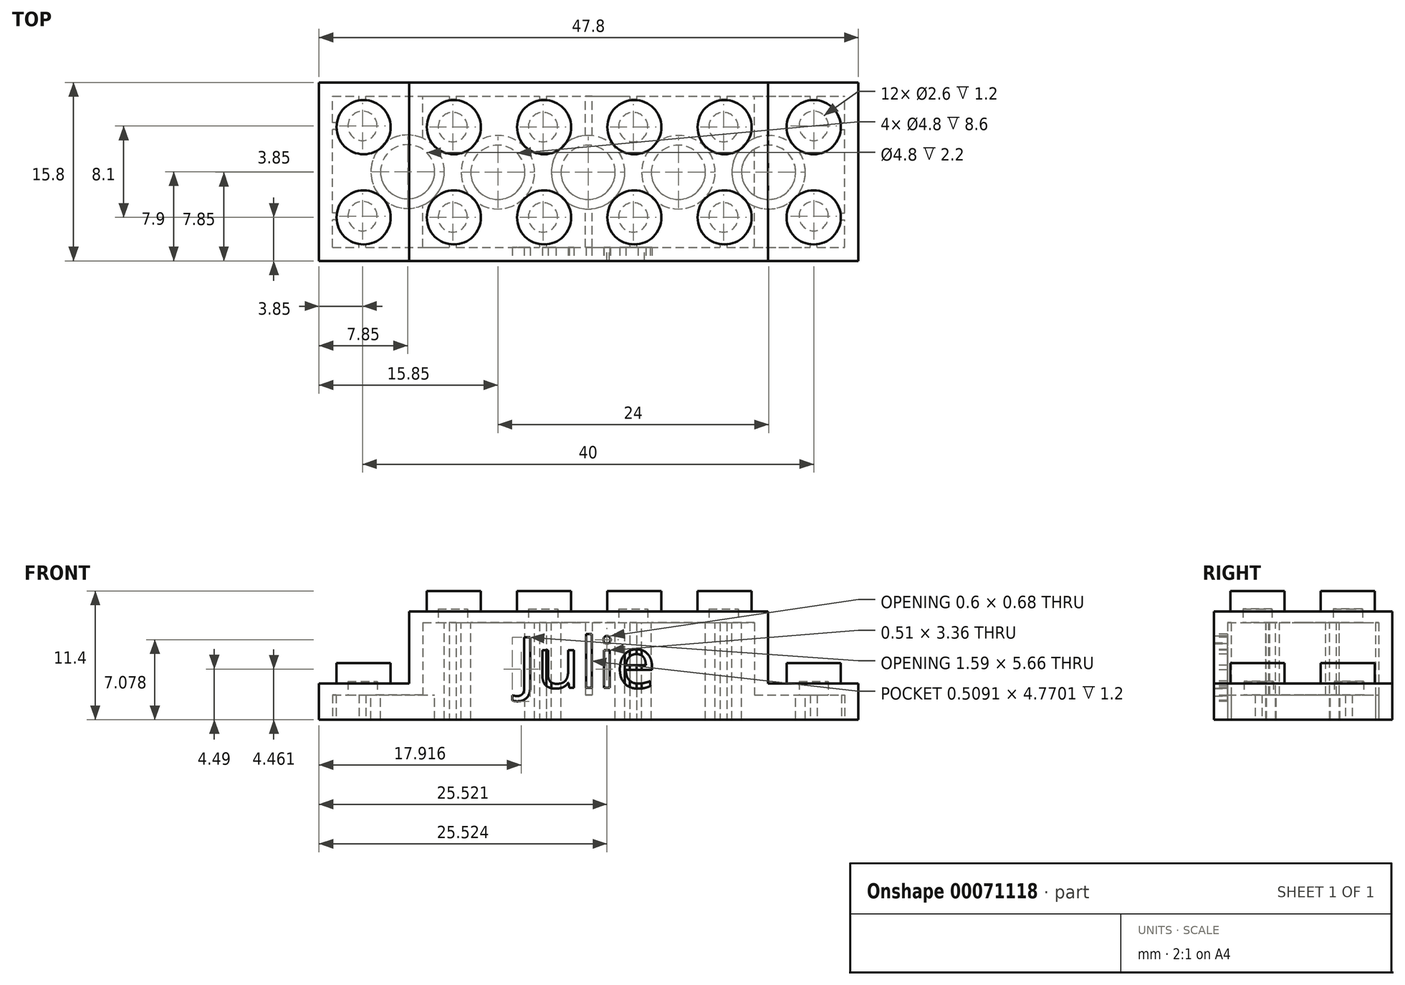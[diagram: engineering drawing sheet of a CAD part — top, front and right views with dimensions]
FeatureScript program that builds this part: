
annotation { "Feature Type Name" : "Feature", "Feature Type Description" : "" }
export const myFeature = defineFeature(function(context is Context, id is Id, definition is map)
    precondition{}
    {
        {
            var Q0;
            Q0=qCreatedBy(makeId("Top.planeOp"),FACE);
            var sketch = newSketch(context, id + "F0", { "sketchPlane" : qUnion([Q0])});
            skLineSegment(sketch, "E0.rect.bottom", {"start": v(-15.9, 7.9) * mm, "end": v(15.9, 7.9) * mm});
            skLineSegment(sketch, "E0.rect.top", {"start": v(-15.9, -7.9) * mm, "end": v(15.9, -7.9) * mm});
            skLineSegment(sketch, "E0.rect.left", {"start": v(-15.9, 7.9) * mm, "end": v(-15.9, -7.9) * mm});
            skLineSegment(sketch, "E0.rect.right", {"start": v(15.9, 7.9) * mm, "end": v(15.9, -7.9) * mm});
            skPoint(sketch, "E0.rect.middle", {"position": v(0, 0) * mm});
            skSolve(sketch);
        }
        {
            var Q0;
            Q0=qCreatedBy(makeId("Top.planeOp"),FACE);
            var sketch = newSketch(context, id + "F1", { "sketchPlane" : qUnion([Q0])});
            skLineSegment(sketch, "E1.bottom", {"start": v(15.9, 7.9) * mm, "end": v(23.9, 7.9) * mm});
            skLineSegment(sketch, "E1.top", {"start": v(15.9, -7.9) * mm, "end": v(23.9, -7.9) * mm});
            skLineSegment(sketch, "E1.left", {"start": v(15.9, 7.9) * mm, "end": v(15.9, -7.9) * mm});
            skLineSegment(sketch, "E1.right", {"start": v(23.9, 7.9) * mm, "end": v(23.9, -7.9) * mm});
            skSolve(sketch);
        }
        {
            var Q0;
            Q0 = qSketchRegion(id + "F0", true);
            extrude(context, id + "F2", {"entities" : qUnion([Q0]), "oppositeDirection" : true, "depth" : 9.6 * mm});
        }
        {
            var Q0;
            Q0 = qSketchRegion(id + "F1", true);
            extrude(context, id + "F3", {"entities" : qUnion([Q0]), "operationType" : NewBodyOperationType.ADD, "oppositeDirection" : true, "depth" : 9.6 * mm});
        }
        {
            var Q0;
            Q0=qCreatedBy(makeId("Top.planeOp"),FACE);
            var sketch = newSketch(context, id + "F4", { "sketchPlane" : qUnion([Q0])});
            skLineSegment(sketch, "E2.bottom", {"start": v(-23.9, 7.9) * mm, "end": v(-15.9, 7.9) * mm});
            skLineSegment(sketch, "E2.top", {"start": v(-23.9, -7.9) * mm, "end": v(-15.9, -7.9) * mm});
            skLineSegment(sketch, "E2.left", {"start": v(-23.9, 7.9) * mm, "end": v(-23.9, -7.9) * mm});
            skLineSegment(sketch, "E2.right", {"start": v(-15.9, 7.9) * mm, "end": v(-15.9, -7.9) * mm});
            skSolve(sketch);
        }
        {
            var Q0;
            Q0 = qSketchRegion(id + "F4", true);
            extrude(context, id + "F5", {"entities" : qUnion([Q0]), "operationType" : NewBodyOperationType.ADD, "oppositeDirection" : true, "depth" : 9.6 * mm});
        }
        {
            var Q0;
            Q0 = qSketchRegion(id + "F4", true);
            extrude(context, id + "F6", {"entities" : qUnion([Q0]), "operationType" : NewBodyOperationType.REMOVE, "oppositeDirection" : true, "depth" : 6.4 * mm});
        }
        {
            var Q0;
            Q0 = qSketchRegion(id + "F1", true);
            extrude(context, id + "F7", {"entities" : qUnion([Q0]), "operationType" : NewBodyOperationType.REMOVE, "oppositeDirection" : true, "depth" : 6.4 * mm});
        }
        {
            var Q0;
            Q0=makeQuery(id+"F2.opExtrude","CAP_FACE",FACE,{"disambiguationData":[OSD([sQuery(id+"F0.wireOp",EDGE,"E0.rect.bottom"),sQuery(id+"F0.wireOp",EDGE,"E0.rect.top"),sQuery(id+"F0.wireOp",EDGE,"E0.rect.left"),sQuery(id+"F0.wireOp",EDGE,"E0.rect.right")])],"isStart":false});
            var sketch = newSketch(context, id + "F8", { "sketchPlane" : qUnion([Q0])});
            skLineSegment(sketch, "E3.rect.bottom", {"start": v(-14.7, 6.7) * mm, "end": v(14.7, 6.7) * mm});
            skLineSegment(sketch, "E3.rect.top", {"start": v(-14.7, -6.7) * mm, "end": v(14.7, -6.7) * mm});
            skLineSegment(sketch, "E3.rect.left", {"start": v(-14.7, 6.7) * mm, "end": v(-14.7, -6.7) * mm});
            skLineSegment(sketch, "E3.rect.right", {"start": v(14.7, 6.7) * mm, "end": v(14.7, -6.7) * mm});
            skPoint(sketch, "E3.rect.middle", {"position": v(0, 0) * mm});
            skSolve(sketch);
        }
        {
            var Q0;
            Q0=makeQuery(id+"F8.imprint","IMPRINT",FACE,{"disambiguationData":[TD([[makeQuery(id+"F8.imprint","IMPRINT",EDGE,{"derivedFrom":sQuery(id+"F8.wireOp",EDGE,"E3.rect.bottom")}),-1.0]])]});
            extrude(context, id + "F9", {"entities" : qUnion([Q0]), "operationType" : NewBodyOperationType.REMOVE, "oppositeDirection" : true, "depth" : 8.6 * mm});
        }
        {
            var Q0;
            Q0=makeQuery(id+"F5.opExtrude","CAP_FACE",FACE,{"disambiguationData":[OSD([sQuery(id+"F4.wireOp",EDGE,"E2.bottom"),sQuery(id+"F4.wireOp",EDGE,"E2.top"),sQuery(id+"F4.wireOp",EDGE,"E2.left"),sQuery(id+"F4.wireOp",EDGE,"E2.right")])],"isStart":false});
            var sketch = newSketch(context, id + "F10", { "sketchPlane" : qUnion([Q0])});
            skLineSegment(sketch, "E4.bottom", {"start": v(-22.7, 6.7) * mm, "end": v(-15.9, 6.7) * mm});
            skLineSegment(sketch, "E4.top", {"start": v(-22.7, -6.7) * mm, "end": v(-15.9, -6.7) * mm});
            skLineSegment(sketch, "E4.left", {"start": v(-22.7, 6.7) * mm, "end": v(-22.7, -6.7) * mm});
            skLineSegment(sketch, "E4.right", {"start": v(-15.9, 6.7) * mm, "end": v(-15.9, -6.7) * mm});
            skSolve(sketch);
        }
        {
            var Q0;
            Q0 = qSketchRegion(id + "F10", true);
            extrude(context, id + "F11", {"entities" : qUnion([Q0]), "operationType" : NewBodyOperationType.REMOVE, "oppositeDirection" : true, "depth" : 2.2 * mm});
        }
        {
            var Q0;
            Q0=makeQuery(id+"F3.opExtrude","CAP_FACE",FACE,{"disambiguationData":[OSD([sQuery(id+"F1.wireOp",EDGE,"E1.bottom"),sQuery(id+"F1.wireOp",EDGE,"E1.top"),sQuery(id+"F1.wireOp",EDGE,"E1.left"),sQuery(id+"F1.wireOp",EDGE,"E1.right")])],"isStart":false});
            var sketch = newSketch(context, id + "F12", { "sketchPlane" : qUnion([Q0])});
            skLineSegment(sketch, "E5.bottom", {"start": v(15.9, 6.7) * mm, "end": v(22.7, 6.7) * mm});
            skLineSegment(sketch, "E5.top", {"start": v(15.9, -6.7) * mm, "end": v(22.7, -6.7) * mm});
            skLineSegment(sketch, "E5.left", {"start": v(15.9, 6.7) * mm, "end": v(15.9, -6.7) * mm});
            skLineSegment(sketch, "E5.right", {"start": v(22.7, 6.7) * mm, "end": v(22.7, -6.7) * mm});
            skSolve(sketch);
        }
        {
            var Q0;
            Q0 = qSketchRegion(id + "F12", true);
            extrude(context, id + "F13", {"entities" : qUnion([Q0]), "operationType" : NewBodyOperationType.REMOVE, "oppositeDirection" : true, "depth" : 2.2 * mm});
        }
        {
            var Q0;
            Q0=makeQuery(id+"F2.opExtrude","CAP_FACE",FACE,{"disambiguationData":[OSD([sQuery(id+"F0.wireOp",EDGE,"E0.rect.bottom"),sQuery(id+"F0.wireOp",EDGE,"E0.rect.top"),sQuery(id+"F0.wireOp",EDGE,"E0.rect.left"),sQuery(id+"F0.wireOp",EDGE,"E0.rect.right")])],"isStart":false});
            var sketch = newSketch(context, id + "F14", { "sketchPlane" : qUnion([Q0])});
            skLineSegment(sketch, "E6.bottom", {"start": v(-15.9, 6.7) * mm, "end": v(-14.7, 6.7) * mm});
            skLineSegment(sketch, "E6.top", {"start": v(-15.9, -6.7) * mm, "end": v(-14.7, -6.7) * mm});
            skLineSegment(sketch, "E6.left", {"start": v(-15.9, 6.7) * mm, "end": v(-15.9, -6.7) * mm});
            skLineSegment(sketch, "E6.right", {"start": v(-14.7, 6.7) * mm, "end": v(-14.7, -6.7) * mm});
            skSolve(sketch);
        }
        {
            var Q0;
            Q0 = qSketchRegion(id + "F14", true);
            extrude(context, id + "F15", {"entities" : qUnion([Q0]), "operationType" : NewBodyOperationType.REMOVE, "oppositeDirection" : true, "depth" : 2.2 * mm});
        }
        {
            var Q0;
            Q0=makeQuery(id+"F2.opExtrude","CAP_FACE",FACE,{"disambiguationData":[OSD([sQuery(id+"F0.wireOp",EDGE,"E0.rect.bottom"),sQuery(id+"F0.wireOp",EDGE,"E0.rect.top"),sQuery(id+"F0.wireOp",EDGE,"E0.rect.left"),sQuery(id+"F0.wireOp",EDGE,"E0.rect.right")])],"isStart":false});
            var sketch = newSketch(context, id + "F16", { "sketchPlane" : qUnion([Q0])});
            skLineSegment(sketch, "E7.bottom", {"start": v(14.7, 6.7) * mm, "end": v(15.9, 6.7) * mm});
            skLineSegment(sketch, "E7.top", {"start": v(14.7, -6.7) * mm, "end": v(15.9, -6.7) * mm});
            skLineSegment(sketch, "E7.left", {"start": v(14.7, 6.7) * mm, "end": v(14.7, -6.7) * mm});
            skLineSegment(sketch, "E7.right", {"start": v(15.9, 6.7) * mm, "end": v(15.9, -6.7) * mm});
            skSolve(sketch);
        }
        {
            var Q0;
            Q0 = qSketchRegion(id + "F16", true);
            extrude(context, id + "F17", {"entities" : qUnion([Q0]), "operationType" : NewBodyOperationType.REMOVE, "oppositeDirection" : true, "depth" : 2.2 * mm});
        }
        {
            var Q0;
            Q0=makeQuery(id+"F2.opExtrude","CAP_FACE",FACE,{"disambiguationData":[OSD([sQuery(id+"F0.wireOp",EDGE,"E0.rect.bottom"),sQuery(id+"F0.wireOp",EDGE,"E0.rect.top"),sQuery(id+"F0.wireOp",EDGE,"E0.rect.left"),sQuery(id+"F0.wireOp",EDGE,"E0.rect.right")])],"isStart":true});
            var sketch = newSketch(context, id + "F18", { "sketchPlane" : qUnion([Q0])});
            skCircle(sketch, "E8", {"center": v(-11.95, 3.95) * mm, "radius": 2.4 * mm});
            skCircle(sketch, "E9.0.1.0", {"center": v(-11.95, -4.05) * mm, "radius": 2.4 * mm});
            skCircle(sketch, "E9.1.0.0", {"center": v(-3.95, 3.95) * mm, "radius": 2.4 * mm});
            skCircle(sketch, "E9.1.1.0", {"center": v(-3.95, -4.05) * mm, "radius": 2.4 * mm});
            skCircle(sketch, "E9.2.0.0", {"center": v(4.05, 3.95) * mm, "radius": 2.4 * mm});
            skCircle(sketch, "E9.2.1.0", {"center": v(4.05, -4.05) * mm, "radius": 2.4 * mm});
            skCircle(sketch, "E9.3.0.0", {"center": v(12.05, 3.95) * mm, "radius": 2.4 * mm});
            skCircle(sketch, "E9.3.1.0", {"center": v(12.05, -4.05) * mm, "radius": 2.4 * mm});
            skLineSegment(sketch, "E9.direction1", {"start": v(-11.95, 3.95) * mm, "end": v(-3.95, 3.95) * mm, "construction": true});
            skLineSegment(sketch, "E9.direction2", {"start": v(-11.95, 3.95) * mm, "end": v(-11.95, -4.05) * mm, "construction": true});
            skSolve(sketch);
        }
        {
            var Q0;
            Q0=makeQuery(id+"F6.boolean.opBoolean","COPY",FACE,{"derivedFrom":makeQuery(id+"F6.opExtrude","CAP_FACE",FACE,{"disambiguationData":[OSD([sQuery(id+"F4.wireOp",EDGE,"E2.bottom"),sQuery(id+"F4.wireOp",EDGE,"E2.top"),sQuery(id+"F4.wireOp",EDGE,"E2.left"),sQuery(id+"F4.wireOp",EDGE,"E2.right")])],"isStart":false})});
            var sketch = newSketch(context, id + "F19", { "sketchPlane" : qUnion([Q0])});
            skCircle(sketch, "E10", {"center": v(-19.95, 3.95) * mm, "radius": 2.4 * mm});
            skCircle(sketch, "E11.0.1.0", {"center": v(-19.95, -4.05) * mm, "radius": 2.4 * mm});
            skLineSegment(sketch, "E11.direction1", {"start": v(-19.95, 3.95) * mm, "end": v(-44.95, 3.95) * mm, "construction": true});
            skLineSegment(sketch, "E11.direction2", {"start": v(-19.95, 3.95) * mm, "end": v(-19.95, -4.05) * mm, "construction": true});
            skSolve(sketch);
        }
        {
            var Q0;
            Q0=makeQuery(id+"F7.boolean.opBoolean","COPY",FACE,{"derivedFrom":makeQuery(id+"F7.opExtrude","CAP_FACE",FACE,{"disambiguationData":[OSD([sQuery(id+"F1.wireOp",EDGE,"E1.bottom"),sQuery(id+"F1.wireOp",EDGE,"E1.top"),sQuery(id+"F1.wireOp",EDGE,"E1.left"),sQuery(id+"F1.wireOp",EDGE,"E1.right")])],"isStart":false})});
            var sketch = newSketch(context, id + "F20", { "sketchPlane" : qUnion([Q0])});
            skCircle(sketch, "E12", {"center": v(19.95, 3.95) * mm, "radius": 2.4 * mm});
            skCircle(sketch, "E13.0.1.0", {"center": v(19.95, -4.05) * mm, "radius": 2.4 * mm});
            skLineSegment(sketch, "E13.direction1", {"start": v(19.95, 3.95) * mm, "end": v(44.95, 3.95) * mm, "construction": true});
            skLineSegment(sketch, "E13.direction2", {"start": v(19.95, 3.95) * mm, "end": v(19.95, -4.05) * mm, "construction": true});
            skSolve(sketch);
        }
        {
            var Q0;
            Q0 = qSketchRegion(id + "F18", true);
            extrude(context, id + "F21", {"entities" : qUnion([Q0]), "operationType" : NewBodyOperationType.ADD, "depth" : 1.8 * mm});
        }
        {
            var Q0;
            Q0 = qSketchRegion(id + "F19", true);
            extrude(context, id + "F22", {"entities" : qUnion([Q0]), "operationType" : NewBodyOperationType.ADD, "depth" : 1.8 * mm});
        }
        {
            var Q0;
            Q0 = qSketchRegion(id + "F20", true);
            extrude(context, id + "F23", {"entities" : qUnion([Q0]), "operationType" : NewBodyOperationType.ADD, "depth" : 1.8 * mm});
        }
        {
            var Q0;
            Q0=makeQuery(id+"F9.boolean.opBoolean","COPY",FACE,{"derivedFrom":makeQuery(id+"F9.opExtrude","CAP_FACE",FACE,{"disambiguationData":[OSD([sQuery(id+"F8.wireOp",EDGE,"E3.rect.bottom"),sQuery(id+"F8.wireOp",EDGE,"E3.rect.top"),sQuery(id+"F8.wireOp",EDGE,"E3.rect.left"),sQuery(id+"F8.wireOp",EDGE,"E3.rect.right")])],"isStart":false})});
            var sketch = newSketch(context, id + "F24", { "sketchPlane" : qUnion([Q0])});
            skCircle(sketch, "E14", {"center": v(-12.05, 4.05) * mm, "radius": 1.3 * mm});
            skCircle(sketch, "E15.0.1.0", {"center": v(-12.05, -3.95) * mm, "radius": 1.3 * mm});
            skCircle(sketch, "E15.1.0.0", {"center": v(-4.05, 4.05) * mm, "radius": 1.3 * mm});
            skCircle(sketch, "E15.1.1.0", {"center": v(-4.05, -3.95) * mm, "radius": 1.3 * mm});
            skCircle(sketch, "E15.2.0.0", {"center": v(3.95, 4.05) * mm, "radius": 1.3 * mm});
            skCircle(sketch, "E15.2.1.0", {"center": v(3.95, -3.95) * mm, "radius": 1.3 * mm});
            skCircle(sketch, "E15.3.0.0", {"center": v(11.95, 4.05) * mm, "radius": 1.3 * mm});
            skCircle(sketch, "E15.3.1.0", {"center": v(11.95, -3.95) * mm, "radius": 1.3 * mm});
            skLineSegment(sketch, "E15.direction1", {"start": v(-12.05, 4.05) * mm, "end": v(-4.05, 4.05) * mm, "construction": true});
            skLineSegment(sketch, "E15.direction2", {"start": v(-12.05, 4.05) * mm, "end": v(-12.05, -3.95) * mm, "construction": true});
            skLineSegment(sketch, "E16", {"start": v(-4.05, -3.95) * mm, "end": v(-12.05, 4.05) * mm, "construction": true});
            skLineSegment(sketch, "E17", {"start": v(-4.05, 4.05) * mm, "end": v(-12.05, -3.95) * mm, "construction": true});
            skLineSegment(sketch, "E18", {"start": v(3.95, -3.95) * mm, "end": v(-4.05, 4.05) * mm, "construction": true});
            skLineSegment(sketch, "E19", {"start": v(3.95, 4.05) * mm, "end": v(-4.05, -3.95) * mm, "construction": true});
            skLineSegment(sketch, "E20", {"start": v(11.95, -3.95) * mm, "end": v(3.95, 4.05) * mm, "construction": true});
            skLineSegment(sketch, "E21", {"start": v(11.95, 4.05) * mm, "end": v(3.95, -3.95) * mm, "construction": true});
            skSolve(sketch);
        }
        {
            var Q0;
            Q0 = qSketchRegion(id + "F24", true);
            extrude(context, id + "F25", {"entities" : qUnion([Q0]), "operationType" : NewBodyOperationType.REMOVE, "oppositeDirection" : true, "depth" : 1.2 * mm});
        }
        {
            var Q0;
            Q0=makeQuery(id+"F15.boolean.opBoolean","MERGE",FACE,{"derivedFrom":[makeQuery(id+"F11.boolean.opBoolean","COPY",FACE,{"derivedFrom":makeQuery(id+"F11.opExtrude","CAP_FACE",FACE,{"disambiguationData":[OSD([sQuery(id+"F10.wireOp",EDGE,"E4.bottom"),sQuery(id+"F10.wireOp",EDGE,"E4.top"),sQuery(id+"F10.wireOp",EDGE,"E4.left"),sQuery(id+"F10.wireOp",EDGE,"E4.right")])],"isStart":false})}),makeQuery(id+"F15.opExtrude","CAP_FACE",FACE,{"disambiguationData":[OSD([sQuery(id+"F14.wireOp",EDGE,"E6.bottom"),sQuery(id+"F14.wireOp",EDGE,"E6.top"),sQuery(id+"F14.wireOp",EDGE,"E6.left"),sQuery(id+"F14.wireOp",EDGE,"E6.right")])],"isStart":false})]});
            var sketch = newSketch(context, id + "F26", { "sketchPlane" : qUnion([Q0])});
            skCircle(sketch, "E22", {"center": v(-20.05, 3.95) * mm, "radius": 1.3 * mm});
            skCircle(sketch, "E23.0.1.0", {"center": v(-20.05, -4.05) * mm, "radius": 1.3 * mm});
            skLineSegment(sketch, "E23.direction1", {"start": v(-20.05, 3.95) * mm, "end": v(-45.05, 3.95) * mm, "construction": true});
            skLineSegment(sketch, "E23.direction2", {"start": v(-20.05, 3.95) * mm, "end": v(-20.05, -4.05) * mm, "construction": true});
            skCircle(sketch, "E24", {"center": v(19.95, 3.95) * mm, "radius": 1.3 * mm});
            skCircle(sketch, "E25.0.1.0", {"center": v(19.95, -4.05) * mm, "radius": 1.3 * mm});
            skLineSegment(sketch, "E25.direction1", {"start": v(19.95, 3.95) * mm, "end": v(44.95, 3.95) * mm, "construction": true});
            skLineSegment(sketch, "E25.direction2", {"start": v(19.95, 3.95) * mm, "end": v(19.95, -4.05) * mm, "construction": true});
            skCircle(sketch, "E26", {"center": v(-12.05, 4.05) * mm, "radius": 1.3 * mm, "construction": true});
            skSolve(sketch);
        }
        {
            var Q0;
            Q0 = qSketchRegion(id + "F26", true);
            extrude(context, id + "F27", {"entities" : qUnion([Q0]), "operationType" : NewBodyOperationType.REMOVE, "oppositeDirection" : true, "depth" : 1.2 * mm});
        }
        {
            var Q0;
            Q0=makeQuery(id+"F15.boolean.opBoolean","MERGE",FACE,{"derivedFrom":[makeQuery(id+"F11.boolean.opBoolean","COPY",FACE,{"derivedFrom":makeQuery(id+"F11.opExtrude","CAP_FACE",FACE,{"disambiguationData":[OSD([sQuery(id+"F10.wireOp",EDGE,"E4.bottom"),sQuery(id+"F10.wireOp",EDGE,"E4.top"),sQuery(id+"F10.wireOp",EDGE,"E4.left"),sQuery(id+"F10.wireOp",EDGE,"E4.right")])],"isStart":false})}),makeQuery(id+"F15.opExtrude","CAP_FACE",FACE,{"disambiguationData":[OSD([sQuery(id+"F14.wireOp",EDGE,"E6.bottom"),sQuery(id+"F14.wireOp",EDGE,"E6.top"),sQuery(id+"F14.wireOp",EDGE,"E6.left"),sQuery(id+"F14.wireOp",EDGE,"E6.right")])],"isStart":false})]});
            var sketch = newSketch(context, id + "F28", { "sketchPlane" : qUnion([Q0])});
            skCircle(sketch, "E27", {"center": v(-12.05, 4.05) * mm, "radius": 1.56 * mm, "construction": true});
            skLineSegment(sketch, "E28", {"start": v(-20.05, -4.05) * mm, "end": v(-12.05, 4.05) * mm, "construction": true});
            skCircle(sketch, "E29", {"center": v(-16.05, 0) * mm, "radius": 2.4 * mm});
            skCircle(sketch, "E30", {"center": v(-16.05, 0) * mm, "radius": 3.25 * mm});
            skCircle(sketch, "E31", {"center": v(11.95, 4.05) * mm, "radius": 1.3 * mm, "construction": true});
            skCircle(sketch, "E32", {"center": v(19.95, -3.95) * mm, "radius": 1.3 * mm, "construction": true});
            skLineSegment(sketch, "E33", {"start": v(11.95, 4.05) * mm, "end": v(19.95, -3.95) * mm, "construction": true});
            skCircle(sketch, "E34", {"center": v(15.95, 0.05) * mm, "radius": 2.4 * mm});
            skCircle(sketch, "E35", {"center": v(15.95, 0.05) * mm, "radius": 3.25 * mm});
            skSolve(sketch);
        }
        {
            var Q0;
            Q0 = qSketchRegion(id + "F28", true);
            var Q1;
            Q1=makeQuery(id+"F5.boolean.opBoolean","MERGE",FACE,{"derivedFrom":[makeQuery(id+"F3.boolean.opBoolean","MERGE",FACE,{"derivedFrom":[makeQuery(id+"F2.opExtrude","CAP_FACE",FACE,{"disambiguationData":[OSD([sQuery(id+"F0.wireOp",EDGE,"E0.rect.bottom"),sQuery(id+"F0.wireOp",EDGE,"E0.rect.top"),sQuery(id+"F0.wireOp",EDGE,"E0.rect.left"),sQuery(id+"F0.wireOp",EDGE,"E0.rect.right")])],"isStart":false}),makeQuery(id+"F3.opExtrude","CAP_FACE",FACE,{"disambiguationData":[OSD([sQuery(id+"F1.wireOp",EDGE,"E1.bottom"),sQuery(id+"F1.wireOp",EDGE,"E1.top"),sQuery(id+"F1.wireOp",EDGE,"E1.left"),sQuery(id+"F1.wireOp",EDGE,"E1.right")])],"isStart":false})]}),makeQuery(id+"F5.opExtrude","CAP_FACE",FACE,{"disambiguationData":[OSD([sQuery(id+"F4.wireOp",EDGE,"E2.bottom"),sQuery(id+"F4.wireOp",EDGE,"E2.top"),sQuery(id+"F4.wireOp",EDGE,"E2.left"),sQuery(id+"F4.wireOp",EDGE,"E2.right")])],"isStart":false})]});
            extrude(context, id + "F29", {"entities" : qUnion([Q0]), "operationType" : NewBodyOperationType.ADD, "endBound" : BoundingType.UP_TO_SURFACE, "endBoundEntityFace" : qUnion([Q1]), "depth" : 3.2 * mm});
        }
        {
            var Q0;
            Q0=makeQuery(id+"F24.imprint","IMPRINT",FACE,{"disambiguationData":[TD([[makeQuery(id+"F24.imprint","IMPRINT",EDGE,{"derivedFrom":sQuery(id+"F24.wireOp",EDGE,"E14")}),-1.0]])]});
            var sketch = newSketch(context, id + "F30", { "sketchPlane" : qUnion([Q0])});
            skArc(sketch, "E36", {"start": v(-14.7, -1.98) * mm, "mid": v(-13.65, 0) * mm, "end": v(-14.7, 1.98) * mm});
            skArc(sketch, "E37", {"start": v(-14.7, -2.96) * mm, "mid": v(-12.8, 0) * mm, "end": v(-14.7, 2.96) * mm});
            skLineSegment(sketch, "E38", {"start": v(-14.7, 2.96) * mm, "end": v(-14.7, -2.96) * mm});
            skArc(sketch, "E39", {"start": v(14.7, 2.1) * mm, "mid": v(13.55, 0.05) * mm, "end": v(14.7, -2) * mm});
            skArc(sketch, "E40", {"start": v(14.7, 3.06) * mm, "mid": v(12.7, 0.05) * mm, "end": v(14.7, -2.96) * mm});
            skLineSegment(sketch, "E41", {"start": v(14.7, 3.06) * mm, "end": v(14.7, 2.1) * mm});
            skLineSegment(sketch, "E42.trimOffspring", {"start": v(14.7, -2) * mm, "end": v(14.7, -2.96) * mm});
            skSolve(sketch);
        }
        {
            var Q0;
            Q0 = qSketchRegion(id + "F30", true);
            var Q1;
            Q1=makeQuery(id+"F29.opExtrude","SWEPT_FACE",FACE,{"disambiguationData":[OSD([sQuery(id+"F28.wireOp",EDGE,"E30")])]});
            extrude(context, id + "F31", {"entities" : qUnion([Q0]), "operationType" : NewBodyOperationType.ADD, "endBoundEntityFace" : qUnion([Q1]), "depth" : 6.4 * mm});
        }
        {
            var Q0;
            Q0 = qSketchRegion(id + "F30", true);
            extrude(context, id + "F32", {"entities" : qUnion([Q0]), "operationType" : NewBodyOperationType.ADD, "depth" : 6.2 * mm});
        }
        {
            var Q0;
            Q0=makeQuery(id+"F24.imprint","IMPRINT",FACE,{"disambiguationData":[TD([[makeQuery(id+"F24.imprint","IMPRINT",EDGE,{"derivedFrom":sQuery(id+"F24.wireOp",EDGE,"E14")}),-1.0]])]});
            var sketch = newSketch(context, id + "F33", { "sketchPlane" : qUnion([Q0])});
            skCircle(sketch, "E43", {"center": v(-8.05, 0.05) * mm, "radius": 2.4 * mm});
            skCircle(sketch, "E44", {"center": v(-8.05, 0.05) * mm, "radius": 3.25 * mm});
            skCircle(sketch, "E45.1.0.0", {"center": v(-0.05, 0.05) * mm, "radius": 3.25 * mm});
            skCircle(sketch, "E45.1.0.1", {"center": v(-0.05, 0.05) * mm, "radius": 2.4 * mm});
            skCircle(sketch, "E45.2.0.0", {"center": v(7.95, 0.05) * mm, "radius": 3.25 * mm});
            skCircle(sketch, "E45.2.0.1", {"center": v(7.95, 0.05) * mm, "radius": 2.4 * mm});
            skLineSegment(sketch, "E45.direction1", {"start": v(-8.05, 0.05) * mm, "end": v(-0.05, 0.05) * mm, "construction": true});
            skSolve(sketch);
        }
        {
            var Q0;
            Q0 = qSketchRegion(id + "F33", true);
            var Q1;
            Q1=makeQuery(id+"F5.boolean.opBoolean","MERGE",FACE,{"derivedFrom":[makeQuery(id+"F3.boolean.opBoolean","MERGE",FACE,{"derivedFrom":[makeQuery(id+"F2.opExtrude","CAP_FACE",FACE,{"disambiguationData":[OSD([sQuery(id+"F0.wireOp",EDGE,"E0.rect.bottom"),sQuery(id+"F0.wireOp",EDGE,"E0.rect.top"),sQuery(id+"F0.wireOp",EDGE,"E0.rect.left"),sQuery(id+"F0.wireOp",EDGE,"E0.rect.right")])],"isStart":false}),makeQuery(id+"F3.opExtrude","CAP_FACE",FACE,{"disambiguationData":[OSD([sQuery(id+"F1.wireOp",EDGE,"E1.bottom"),sQuery(id+"F1.wireOp",EDGE,"E1.top"),sQuery(id+"F1.wireOp",EDGE,"E1.left"),sQuery(id+"F1.wireOp",EDGE,"E1.right")])],"isStart":false})]}),makeQuery(id+"F5.opExtrude","CAP_FACE",FACE,{"disambiguationData":[OSD([sQuery(id+"F4.wireOp",EDGE,"E2.bottom"),sQuery(id+"F4.wireOp",EDGE,"E2.top"),sQuery(id+"F4.wireOp",EDGE,"E2.left"),sQuery(id+"F4.wireOp",EDGE,"E2.right")])],"isStart":false})]});
            extrude(context, id + "F34", {"entities" : qUnion([Q0]), "operationType" : NewBodyOperationType.ADD, "endBound" : BoundingType.UP_TO_SURFACE, "endBoundEntityFace" : qUnion([Q1]), "depth" : 25 * mm});
        }
        {
            var Q0;
            Q0=makeQuery(id+"F5.boolean.opBoolean","MERGE",FACE,{"derivedFrom":[makeQuery(id+"F3.boolean.opBoolean","MERGE",FACE,{"derivedFrom":[makeQuery(id+"F2.opExtrude","CAP_FACE",FACE,{"disambiguationData":[OSD([sQuery(id+"F0.wireOp",EDGE,"E0.rect.bottom"),sQuery(id+"F0.wireOp",EDGE,"E0.rect.top"),sQuery(id+"F0.wireOp",EDGE,"E0.rect.left"),sQuery(id+"F0.wireOp",EDGE,"E0.rect.right")])],"isStart":false}),makeQuery(id+"F3.opExtrude","CAP_FACE",FACE,{"disambiguationData":[OSD([sQuery(id+"F1.wireOp",EDGE,"E1.bottom"),sQuery(id+"F1.wireOp",EDGE,"E1.top"),sQuery(id+"F1.wireOp",EDGE,"E1.left"),sQuery(id+"F1.wireOp",EDGE,"E1.right")])],"isStart":false})]}),makeQuery(id+"F5.opExtrude","CAP_FACE",FACE,{"disambiguationData":[OSD([sQuery(id+"F4.wireOp",EDGE,"E2.bottom"),sQuery(id+"F4.wireOp",EDGE,"E2.top"),sQuery(id+"F4.wireOp",EDGE,"E2.left"),sQuery(id+"F4.wireOp",EDGE,"E2.right")])],"isStart":false})]});
            var sketch = newSketch(context, id + "F35", { "sketchPlane" : qUnion([Q0])});
            skLineSegment(sketch, "E46.bottom", {"start": v(-22.7, 4.25) * mm, "end": v(-22.4, 4.25) * mm});
            skLineSegment(sketch, "E46.top", {"start": v(-22.7, 3.65) * mm, "end": v(-22.4, 3.65) * mm});
            skLineSegment(sketch, "E46.left", {"start": v(-22.7, 4.25) * mm, "end": v(-22.7, 3.65) * mm});
            skLineSegment(sketch, "E46.right", {"start": v(-22.4, 4.25) * mm, "end": v(-22.4, 3.65) * mm});
            skLineSegment(sketch, "E47.0.1.0", {"start": v(-22.7, -3.75) * mm, "end": v(-22.4, -3.75) * mm});
            skLineSegment(sketch, "E47.0.1.1", {"start": v(-22.4, -3.75) * mm, "end": v(-22.4, -4.35) * mm});
            skLineSegment(sketch, "E47.0.1.2", {"start": v(-22.7, -4.35) * mm, "end": v(-22.4, -4.35) * mm});
            skLineSegment(sketch, "E47.0.1.3", {"start": v(-22.7, -3.75) * mm, "end": v(-22.7, -4.35) * mm});
            skLineSegment(sketch, "E47.direction1", {"start": v(-22.7, 4.25) * mm, "end": v(2.3, 4.25) * mm, "construction": true});
            skLineSegment(sketch, "E47.direction2", {"start": v(-22.7, 4.25) * mm, "end": v(-22.7, -3.75) * mm, "construction": true});
            skSolve(sketch);
        }
        {
            var Q0;
            Q0 = qSketchRegion(id + "F35", true);
            var Q1;
            {var subQ0=sQuery(id+"F14.wireOp",EDGE,"E6.bottom");var subQ1=sQuery(id+"F10.wireOp",EDGE,"E4.left");var subQ2=sQuery(id+"F10.wireOp",EDGE,"E4.top");var subQ3=sQuery(id+"F10.wireOp",EDGE,"E4.bottom");var subQ4=sQuery(id+"F14.wireOp",EDGE,"E6.top");Q1=makeQuery(id+"F29.boolean.opBoolean","SPLIT",FACE,{"disambiguationData":[TD([makeQuery(id+"F9.boolean.opBoolean","COPY",FACE,{"derivedFrom":makeQuery(id+"F9.opExtrude","SWEPT_FACE",FACE,{"disambiguationData":[OSD([sQuery(id+"F8.wireOp",EDGE,"E3.rect.bottom")])]})})])],"derivedFrom":makeQuery(id+"F15.boolean.opBoolean","MERGE",FACE,{"derivedFrom":[makeQuery(id+"F11.boolean.opBoolean","COPY",FACE,{"derivedFrom":makeQuery(id+"F11.opExtrude","CAP_FACE",FACE,{"disambiguationData":[OSD([subQ3,subQ2,subQ1,sQuery(id+"F10.wireOp",EDGE,"E4.right")])],"isStart":false})}),makeQuery(id+"F15.opExtrude","CAP_FACE",FACE,{"disambiguationData":[OSD([subQ0,subQ4,sQuery(id+"F14.wireOp",EDGE,"E6.left"),sQuery(id+"F14.wireOp",EDGE,"E6.right")])],"isStart":false})]})});}
            extrude(context, id + "F36", {"entities" : qUnion([Q0]), "operationType" : NewBodyOperationType.ADD, "endBound" : BoundingType.UP_TO_SURFACE, "oppositeDirection" : true, "endBoundEntityFace" : qUnion([Q1]), "depth" : 25 * mm});
        }
        {
            var Q0;
            Q0=makeQuery(id+"F36.boolean.opBoolean","MERGE",FACE,{"derivedFrom":[makeQuery(id+"F5.boolean.opBoolean","MERGE",FACE,{"derivedFrom":[makeQuery(id+"F3.boolean.opBoolean","MERGE",FACE,{"derivedFrom":[makeQuery(id+"F2.opExtrude","CAP_FACE",FACE,{"disambiguationData":[OSD([sQuery(id+"F0.wireOp",EDGE,"E0.rect.bottom"),sQuery(id+"F0.wireOp",EDGE,"E0.rect.top"),sQuery(id+"F0.wireOp",EDGE,"E0.rect.left"),sQuery(id+"F0.wireOp",EDGE,"E0.rect.right")])],"isStart":false}),makeQuery(id+"F3.opExtrude","CAP_FACE",FACE,{"disambiguationData":[OSD([sQuery(id+"F1.wireOp",EDGE,"E1.bottom"),sQuery(id+"F1.wireOp",EDGE,"E1.top"),sQuery(id+"F1.wireOp",EDGE,"E1.left"),sQuery(id+"F1.wireOp",EDGE,"E1.right")])],"isStart":false})]}),makeQuery(id+"F5.opExtrude","CAP_FACE",FACE,{"disambiguationData":[OSD([sQuery(id+"F4.wireOp",EDGE,"E2.bottom"),sQuery(id+"F4.wireOp",EDGE,"E2.top"),sQuery(id+"F4.wireOp",EDGE,"E2.left"),sQuery(id+"F4.wireOp",EDGE,"E2.right")])],"isStart":false})]}),makeQuery(id+"F36.opExtrude","CAP_FACE",FACE,{"disambiguationData":[OSD([sQuery(id+"F35.wireOp",EDGE,"E46.bottom"),sQuery(id+"F35.wireOp",EDGE,"E46.top"),sQuery(id+"F35.wireOp",EDGE,"E46.left"),sQuery(id+"F35.wireOp",EDGE,"E46.right")])],"isStart":true}),makeQuery(id+"F36.opExtrude","CAP_FACE",FACE,{"disambiguationData":[OSD([sQuery(id+"F35.wireOp",EDGE,"E47.0.1.0"),sQuery(id+"F35.wireOp",EDGE,"E47.0.1.1"),sQuery(id+"F35.wireOp",EDGE,"E47.0.1.2"),sQuery(id+"F35.wireOp",EDGE,"E47.0.1.3")])],"isStart":true})]});
            var sketch = newSketch(context, id + "F37", { "sketchPlane" : qUnion([Q0])});
            skLineSegment(sketch, "E48.bottom", {"start": v(22.4, 4.25) * mm, "end": v(22.7, 4.25) * mm});
            skLineSegment(sketch, "E48.top", {"start": v(22.4, 3.65) * mm, "end": v(22.7, 3.65) * mm});
            skLineSegment(sketch, "E48.left", {"start": v(22.4, 4.25) * mm, "end": v(22.4, 3.65) * mm});
            skLineSegment(sketch, "E48.right", {"start": v(22.7, 4.25) * mm, "end": v(22.7, 3.65) * mm});
            skLineSegment(sketch, "E49.0.1.0", {"start": v(22.4, -3.75) * mm, "end": v(22.7, -3.75) * mm});
            skLineSegment(sketch, "E49.0.1.1", {"start": v(22.7, -3.75) * mm, "end": v(22.7, -4.35) * mm});
            skLineSegment(sketch, "E49.0.1.2", {"start": v(22.4, -4.35) * mm, "end": v(22.7, -4.35) * mm});
            skLineSegment(sketch, "E49.0.1.3", {"start": v(22.4, -3.75) * mm, "end": v(22.4, -4.35) * mm});
            skLineSegment(sketch, "E49.direction1", {"start": v(22.4, 4.25) * mm, "end": v(47.4, 4.25) * mm, "construction": true});
            skLineSegment(sketch, "E49.direction2", {"start": v(22.4, 4.25) * mm, "end": v(22.4, -3.75) * mm, "construction": true});
            skSolve(sketch);
        }
        {
            var Q0;
            Q0 = qSketchRegion(id + "F37", true);
            extrude(context, id + "F38", {"entities" : qUnion([Q0]), "operationType" : NewBodyOperationType.ADD, "oppositeDirection" : true, "depth" : 3.2 * mm});
        }
        {
            var Q0;
            Q0=makeQuery(id+"F38.boolean.opBoolean","MERGE",FACE,{"derivedFrom":[makeQuery(id+"F36.boolean.opBoolean","MERGE",FACE,{"derivedFrom":[makeQuery(id+"F5.boolean.opBoolean","MERGE",FACE,{"derivedFrom":[makeQuery(id+"F3.boolean.opBoolean","MERGE",FACE,{"derivedFrom":[makeQuery(id+"F2.opExtrude","CAP_FACE",FACE,{"disambiguationData":[OSD([sQuery(id+"F0.wireOp",EDGE,"E0.rect.bottom"),sQuery(id+"F0.wireOp",EDGE,"E0.rect.top"),sQuery(id+"F0.wireOp",EDGE,"E0.rect.left"),sQuery(id+"F0.wireOp",EDGE,"E0.rect.right")])],"isStart":false}),makeQuery(id+"F3.opExtrude","CAP_FACE",FACE,{"disambiguationData":[OSD([sQuery(id+"F1.wireOp",EDGE,"E1.bottom"),sQuery(id+"F1.wireOp",EDGE,"E1.top"),sQuery(id+"F1.wireOp",EDGE,"E1.left"),sQuery(id+"F1.wireOp",EDGE,"E1.right")])],"isStart":false})]}),makeQuery(id+"F5.opExtrude","CAP_FACE",FACE,{"disambiguationData":[OSD([sQuery(id+"F4.wireOp",EDGE,"E2.bottom"),sQuery(id+"F4.wireOp",EDGE,"E2.top"),sQuery(id+"F4.wireOp",EDGE,"E2.left"),sQuery(id+"F4.wireOp",EDGE,"E2.right")])],"isStart":false})]}),makeQuery(id+"F36.opExtrude","CAP_FACE",FACE,{"disambiguationData":[OSD([sQuery(id+"F35.wireOp",EDGE,"E46.bottom"),sQuery(id+"F35.wireOp",EDGE,"E46.top"),sQuery(id+"F35.wireOp",EDGE,"E46.left"),sQuery(id+"F35.wireOp",EDGE,"E46.right")])],"isStart":true}),makeQuery(id+"F36.opExtrude","CAP_FACE",FACE,{"disambiguationData":[OSD([sQuery(id+"F35.wireOp",EDGE,"E47.0.1.0"),sQuery(id+"F35.wireOp",EDGE,"E47.0.1.1"),sQuery(id+"F35.wireOp",EDGE,"E47.0.1.2"),sQuery(id+"F35.wireOp",EDGE,"E47.0.1.3")])],"isStart":true})]}),makeQuery(id+"F38.opExtrude","CAP_FACE",FACE,{"disambiguationData":[OSD([sQuery(id+"F37.wireOp",EDGE,"E48.bottom"),sQuery(id+"F37.wireOp",EDGE,"E48.top"),sQuery(id+"F37.wireOp",EDGE,"E48.left"),sQuery(id+"F37.wireOp",EDGE,"E48.right")])],"isStart":true}),makeQuery(id+"F38.opExtrude","CAP_FACE",FACE,{"disambiguationData":[OSD([sQuery(id+"F37.wireOp",EDGE,"E49.0.1.0"),sQuery(id+"F37.wireOp",EDGE,"E49.0.1.1"),sQuery(id+"F37.wireOp",EDGE,"E49.0.1.2"),sQuery(id+"F37.wireOp",EDGE,"E49.0.1.3")])],"isStart":true})]});
            var sketch = newSketch(context, id + "F39", { "sketchPlane" : qUnion([Q0])});
            skLineSegment(sketch, "E50.bottom", {"start": v(19.65, 6.7) * mm, "end": v(20.25, 6.7) * mm});
            skLineSegment(sketch, "E50.top", {"start": v(19.65, 6.4) * mm, "end": v(20.25, 6.4) * mm});
            skLineSegment(sketch, "E50.left", {"start": v(19.65, 6.7) * mm, "end": v(19.65, 6.4) * mm});
            skLineSegment(sketch, "E50.right", {"start": v(20.25, 6.7) * mm, "end": v(20.25, 6.4) * mm});
            skLineSegment(sketch, "E51.bottom", {"start": v(-20.35, 6.7) * mm, "end": v(-19.75, 6.7) * mm});
            skLineSegment(sketch, "E51.top", {"start": v(-20.35, 6.4) * mm, "end": v(-19.75, 6.4) * mm});
            skLineSegment(sketch, "E51.left", {"start": v(-20.35, 6.7) * mm, "end": v(-20.35, 6.4) * mm});
            skLineSegment(sketch, "E51.right", {"start": v(-19.75, 6.7) * mm, "end": v(-19.75, 6.4) * mm});
            skLineSegment(sketch, "E52.bottom", {"start": v(-20.35, -6.4) * mm, "end": v(-19.75, -6.4) * mm});
            skLineSegment(sketch, "E52.top", {"start": v(-20.35, -6.7) * mm, "end": v(-19.75, -6.7) * mm});
            skLineSegment(sketch, "E52.left", {"start": v(-20.35, -6.4) * mm, "end": v(-20.35, -6.7) * mm});
            skLineSegment(sketch, "E52.right", {"start": v(-19.75, -6.4) * mm, "end": v(-19.75, -6.7) * mm});
            skLineSegment(sketch, "E53.bottom", {"start": v(19.65, -6.4) * mm, "end": v(20.25, -6.4) * mm});
            skLineSegment(sketch, "E53.top", {"start": v(19.65, -6.7) * mm, "end": v(20.25, -6.7) * mm});
            skLineSegment(sketch, "E53.left", {"start": v(19.65, -6.4) * mm, "end": v(19.65, -6.7) * mm});
            skLineSegment(sketch, "E53.right", {"start": v(20.25, -6.4) * mm, "end": v(20.25, -6.7) * mm});
            skSolve(sketch);
        }
        {
            var Q0;
            Q0 = qSketchRegion(id + "F39", true);
            extrude(context, id + "F40", {"entities" : qUnion([Q0]), "operationType" : NewBodyOperationType.ADD, "oppositeDirection" : true, "depth" : 3.2 * mm});
        }
        {
            var Q0;
            Q0 = qSketchRegion(id + "F39", true);
            extrude(context, id + "F41", {"entities" : qUnion([Q0]), "operationType" : NewBodyOperationType.ADD, "oppositeDirection" : true, "depth" : 3.2 * mm});
        }
        {
            var Q0;
            Q0 = qSketchRegion(id + "F39", true);
            extrude(context, id + "F42", {"entities" : qUnion([Q0]), "operationType" : NewBodyOperationType.ADD, "oppositeDirection" : true, "depth" : 3.2 * mm});
        }
        {
            var Q0;
            Q0 = qSketchRegion(id + "F39", true);
            extrude(context, id + "F43", {"entities" : qUnion([Q0]), "operationType" : NewBodyOperationType.ADD, "oppositeDirection" : true, "depth" : 3.2 * mm});
        }
        {
            var Q0;
            Q0=makeQuery(id+"F40.boolean.opBoolean","MERGE",FACE,{"derivedFrom":[makeQuery(id+"F38.boolean.opBoolean","MERGE",FACE,{"derivedFrom":[makeQuery(id+"F36.boolean.opBoolean","MERGE",FACE,{"derivedFrom":[makeQuery(id+"F5.boolean.opBoolean","MERGE",FACE,{"derivedFrom":[makeQuery(id+"F3.boolean.opBoolean","MERGE",FACE,{"derivedFrom":[makeQuery(id+"F2.opExtrude","CAP_FACE",FACE,{"disambiguationData":[OSD([sQuery(id+"F0.wireOp",EDGE,"E0.rect.bottom"),sQuery(id+"F0.wireOp",EDGE,"E0.rect.top"),sQuery(id+"F0.wireOp",EDGE,"E0.rect.left"),sQuery(id+"F0.wireOp",EDGE,"E0.rect.right")])],"isStart":false}),makeQuery(id+"F3.opExtrude","CAP_FACE",FACE,{"disambiguationData":[OSD([sQuery(id+"F1.wireOp",EDGE,"E1.bottom"),sQuery(id+"F1.wireOp",EDGE,"E1.top"),sQuery(id+"F1.wireOp",EDGE,"E1.left"),sQuery(id+"F1.wireOp",EDGE,"E1.right")])],"isStart":false})]}),makeQuery(id+"F5.opExtrude","CAP_FACE",FACE,{"disambiguationData":[OSD([sQuery(id+"F4.wireOp",EDGE,"E2.bottom"),sQuery(id+"F4.wireOp",EDGE,"E2.top"),sQuery(id+"F4.wireOp",EDGE,"E2.left"),sQuery(id+"F4.wireOp",EDGE,"E2.right")])],"isStart":false})]}),makeQuery(id+"F36.opExtrude","CAP_FACE",FACE,{"disambiguationData":[OSD([sQuery(id+"F35.wireOp",EDGE,"E46.bottom"),sQuery(id+"F35.wireOp",EDGE,"E46.top"),sQuery(id+"F35.wireOp",EDGE,"E46.left"),sQuery(id+"F35.wireOp",EDGE,"E46.right")])],"isStart":true}),makeQuery(id+"F36.opExtrude","CAP_FACE",FACE,{"disambiguationData":[OSD([sQuery(id+"F35.wireOp",EDGE,"E47.0.1.0"),sQuery(id+"F35.wireOp",EDGE,"E47.0.1.1"),sQuery(id+"F35.wireOp",EDGE,"E47.0.1.2"),sQuery(id+"F35.wireOp",EDGE,"E47.0.1.3")])],"isStart":true})]}),makeQuery(id+"F38.opExtrude","CAP_FACE",FACE,{"disambiguationData":[OSD([sQuery(id+"F37.wireOp",EDGE,"E48.bottom"),sQuery(id+"F37.wireOp",EDGE,"E48.top"),sQuery(id+"F37.wireOp",EDGE,"E48.left"),sQuery(id+"F37.wireOp",EDGE,"E48.right")])],"isStart":true}),makeQuery(id+"F38.opExtrude","CAP_FACE",FACE,{"disambiguationData":[OSD([sQuery(id+"F37.wireOp",EDGE,"E49.0.1.0"),sQuery(id+"F37.wireOp",EDGE,"E49.0.1.1"),sQuery(id+"F37.wireOp",EDGE,"E49.0.1.2"),sQuery(id+"F37.wireOp",EDGE,"E49.0.1.3")])],"isStart":true})]}),makeQuery(id+"F40.opExtrude","CAP_FACE",FACE,{"disambiguationData":[OSD([sQuery(id+"F39.wireOp",EDGE,"E50.bottom"),sQuery(id+"F39.wireOp",EDGE,"E50.top"),sQuery(id+"F39.wireOp",EDGE,"E50.left"),sQuery(id+"F39.wireOp",EDGE,"E50.right")])],"isStart":true}),makeQuery(id+"F40.opExtrude","CAP_FACE",FACE,{"disambiguationData":[OSD([sQuery(id+"F39.wireOp",EDGE,"E51.bottom"),sQuery(id+"F39.wireOp",EDGE,"E51.top"),sQuery(id+"F39.wireOp",EDGE,"E51.left"),sQuery(id+"F39.wireOp",EDGE,"E51.right")])],"isStart":true}),makeQuery(id+"F40.opExtrude","CAP_FACE",FACE,{"disambiguationData":[OSD([sQuery(id+"F39.wireOp",EDGE,"E52.bottom"),sQuery(id+"F39.wireOp",EDGE,"E52.top"),sQuery(id+"F39.wireOp",EDGE,"E52.left"),sQuery(id+"F39.wireOp",EDGE,"E52.right")])],"isStart":true}),makeQuery(id+"F40.opExtrude","CAP_FACE",FACE,{"disambiguationData":[OSD([sQuery(id+"F39.wireOp",EDGE,"E53.bottom"),sQuery(id+"F39.wireOp",EDGE,"E53.top"),sQuery(id+"F39.wireOp",EDGE,"E53.left"),sQuery(id+"F39.wireOp",EDGE,"E53.right")])],"isStart":true})]});
            var sketch = newSketch(context, id + "F44", { "sketchPlane" : qUnion([Q0])});
            skLineSegment(sketch, "E54.bottom", {"start": v(-12.35, 6.7) * mm, "end": v(-11.75, 6.7) * mm});
            skLineSegment(sketch, "E54.top", {"start": v(-12.35, 6.4) * mm, "end": v(-11.75, 6.4) * mm});
            skLineSegment(sketch, "E54.left", {"start": v(-12.35, 6.7) * mm, "end": v(-12.35, 6.4) * mm});
            skLineSegment(sketch, "E54.right", {"start": v(-11.75, 6.7) * mm, "end": v(-11.75, 6.4) * mm});
            skLineSegment(sketch, "E55.0.1.0", {"start": v(-11.75, -6.4) * mm, "end": v(-11.75, -6.7) * mm});
            skLineSegment(sketch, "E55.0.1.1", {"start": v(-12.35, -6.4) * mm, "end": v(-11.75, -6.4) * mm});
            skLineSegment(sketch, "E55.0.1.2", {"start": v(-12.35, -6.7) * mm, "end": v(-11.75, -6.7) * mm});
            skLineSegment(sketch, "E55.0.1.3", {"start": v(-12.35, -6.4) * mm, "end": v(-12.35, -6.7) * mm});
            skLineSegment(sketch, "E55.1.0.0", {"start": v(-3.75, 6.7) * mm, "end": v(-3.75, 6.4) * mm});
            skLineSegment(sketch, "E55.1.0.1", {"start": v(-4.35, 6.7) * mm, "end": v(-3.75, 6.7) * mm});
            skLineSegment(sketch, "E55.1.0.2", {"start": v(-4.35, 6.4) * mm, "end": v(-3.75, 6.4) * mm});
            skLineSegment(sketch, "E55.1.0.3", {"start": v(-4.35, 6.7) * mm, "end": v(-4.35, 6.4) * mm});
            skLineSegment(sketch, "E55.1.1.0", {"start": v(-3.75, -6.4) * mm, "end": v(-3.75, -6.7) * mm});
            skLineSegment(sketch, "E55.1.1.1", {"start": v(-4.35, -6.4) * mm, "end": v(-3.75, -6.4) * mm});
            skLineSegment(sketch, "E55.1.1.2", {"start": v(-4.35, -6.7) * mm, "end": v(-3.75, -6.7) * mm});
            skLineSegment(sketch, "E55.1.1.3", {"start": v(-4.35, -6.4) * mm, "end": v(-4.35, -6.7) * mm});
            skLineSegment(sketch, "E55.2.0.0", {"start": v(4.25, 6.7) * mm, "end": v(4.25, 6.4) * mm});
            skLineSegment(sketch, "E55.2.0.1", {"start": v(3.65, 6.7) * mm, "end": v(4.25, 6.7) * mm});
            skLineSegment(sketch, "E55.2.0.2", {"start": v(3.65, 6.4) * mm, "end": v(4.25, 6.4) * mm});
            skLineSegment(sketch, "E55.2.0.3", {"start": v(3.65, 6.7) * mm, "end": v(3.65, 6.4) * mm});
            skLineSegment(sketch, "E55.2.1.0", {"start": v(4.25, -6.4) * mm, "end": v(4.25, -6.7) * mm});
            skLineSegment(sketch, "E55.2.1.1", {"start": v(3.65, -6.4) * mm, "end": v(4.25, -6.4) * mm});
            skLineSegment(sketch, "E55.2.1.2", {"start": v(3.65, -6.7) * mm, "end": v(4.25, -6.7) * mm});
            skLineSegment(sketch, "E55.2.1.3", {"start": v(3.65, -6.4) * mm, "end": v(3.65, -6.7) * mm});
            skLineSegment(sketch, "E55.3.0.0", {"start": v(12.25, 6.7) * mm, "end": v(12.25, 6.4) * mm});
            skLineSegment(sketch, "E55.3.0.1", {"start": v(11.65, 6.7) * mm, "end": v(12.25, 6.7) * mm});
            skLineSegment(sketch, "E55.3.0.2", {"start": v(11.65, 6.4) * mm, "end": v(12.25, 6.4) * mm});
            skLineSegment(sketch, "E55.3.0.3", {"start": v(11.65, 6.7) * mm, "end": v(11.65, 6.4) * mm});
            skLineSegment(sketch, "E55.3.1.0", {"start": v(12.25, -6.4) * mm, "end": v(12.25, -6.7) * mm});
            skLineSegment(sketch, "E55.3.1.1", {"start": v(11.65, -6.4) * mm, "end": v(12.25, -6.4) * mm});
            skLineSegment(sketch, "E55.3.1.2", {"start": v(11.65, -6.7) * mm, "end": v(12.25, -6.7) * mm});
            skLineSegment(sketch, "E55.3.1.3", {"start": v(11.65, -6.4) * mm, "end": v(11.65, -6.7) * mm});
            skLineSegment(sketch, "E55.direction1", {"start": v(-11.75, 6.4) * mm, "end": v(-3.75, 6.4) * mm, "construction": true});
            skLineSegment(sketch, "E55.direction2", {"start": v(-11.75, 6.4) * mm, "end": v(-11.75, -6.7) * mm, "construction": true});
            skSolve(sketch);
        }
        {
            var Q0;
            Q0 = qSketchRegion(id + "F44", true);
            var Q1;
            {var subQ12=sQuery(id+"F8.wireOp",EDGE,"E3.rect.right");var subQ14=sQuery(id+"F8.wireOp",EDGE,"E3.rect.left");var subQ18=sQuery(id+"F8.wireOp",EDGE,"E3.rect.top");var subQ21=sQuery(id+"F8.wireOp",EDGE,"E3.rect.bottom");var subQ22=makeQuery(id+"F9.boolean.opBoolean","COPY",FACE,{"derivedFrom":makeQuery(id+"F9.opExtrude","SWEPT_FACE",FACE,{"disambiguationData":[OSD([subQ21])]})});Q1=makeQuery(id+"F34.boolean.opBoolean","SPLIT",FACE,{"disambiguationData":[TD([subQ22])],"derivedFrom":makeQuery(id+"F31.boolean.opBoolean","SPLIT",FACE,{"disambiguationData":[TD([subQ22])],"derivedFrom":makeQuery(id+"F9.boolean.opBoolean","COPY",FACE,{"derivedFrom":makeQuery(id+"F9.opExtrude","CAP_FACE",FACE,{"disambiguationData":[OSD([subQ21,subQ18,subQ14,subQ12])],"isStart":false})})})});}
            extrude(context, id + "F45", {"entities" : qUnion([Q0]), "operationType" : NewBodyOperationType.ADD, "endBound" : BoundingType.UP_TO_SURFACE, "oppositeDirection" : true, "endBoundEntityFace" : qUnion([Q1]), "depth" : 25 * mm});
        }
        {
            var Q0;
            Q0=makeQuery(id+"F24.imprint","IMPRINT",FACE,{"disambiguationData":[TD([[makeQuery(id+"F24.imprint","IMPRINT",EDGE,{"derivedFrom":sQuery(id+"F24.wireOp",EDGE,"E14")}),-1.0]])]});
            var sketch = newSketch(context, id + "F46", { "sketchPlane" : qUnion([Q0])});
            skLineSegment(sketch, "E56.bottom", {"start": v(-0.3, 7.05) * mm, "end": v(0.3, 7.05) * mm});
            skLineSegment(sketch, "E56.top", {"start": v(-0.3, 3.05) * mm, "end": v(0.3, 3.05) * mm});
            skLineSegment(sketch, "E56.left", {"start": v(-0.3, 7.05) * mm, "end": v(-0.3, 3.05) * mm});
            skLineSegment(sketch, "E56.right", {"start": v(0.3, 7.05) * mm, "end": v(0.3, 3.05) * mm});
            skLineSegment(sketch, "E57.bottom", {"start": v(-0.3, -2.83) * mm, "end": v(0.3, -2.83) * mm});
            skLineSegment(sketch, "E57.top", {"start": v(-0.3, -7.03) * mm, "end": v(0.3, -7.03) * mm});
            skLineSegment(sketch, "E57.left", {"start": v(-0.3, -2.83) * mm, "end": v(-0.3, -7.03) * mm});
            skLineSegment(sketch, "E57.right", {"start": v(0.3, -2.83) * mm, "end": v(0.3, -7.03) * mm});
            skSolve(sketch);
        }
        {
            var Q0;
            Q0 = qSketchRegion(id + "F46", true);
            extrude(context, id + "F47", {"entities" : qUnion([Q0]), "operationType" : NewBodyOperationType.ADD, "depth" : 6.4 * mm});
        }
        {
            var Q0;
            Q0 = qSketchRegion(id + "F46", true);
            extrude(context, id + "F48", {"entities" : qUnion([Q0]), "operationType" : NewBodyOperationType.ADD, "depth" : 6.4 * mm});
        }
        {
            var Q0;
            Q0=makeQuery(id+"F5.boolean.opBoolean","MERGE",FACE,{"derivedFrom":[makeQuery(id+"F3.boolean.opBoolean","MERGE",FACE,{"derivedFrom":[makeQuery(id+"F2.opExtrude","SWEPT_FACE",FACE,{"disambiguationData":[OSD([sQuery(id+"F0.wireOp",EDGE,"E0.rect.top")])]}),makeQuery(id+"F3.opExtrude","SWEPT_FACE",FACE,{"disambiguationData":[OSD([sQuery(id+"F1.wireOp",EDGE,"E1.top")])]})]}),makeQuery(id+"F5.opExtrude","SWEPT_FACE",FACE,{"disambiguationData":[OSD([sQuery(id+"F4.wireOp",EDGE,"E2.top")])]})]});
            var sketch = newSketch(context, id + "F49", { "sketchPlane" : qUnion([Q0])});
            skText(sketch, "E58", { "text": "Julie\n", "fontName": "OpenSans-Regular.ttf"});
            const initialGuessF49  = {"E58": [-0.00629, -0.00679, 1, 0, 0.00452]};
            skSetInitialGuess(sketch, initialGuessF49);
            skSolve(sketch);
        }
        {
            var Q0;
            Q0 = qSketchRegion(id + "F49", true);
            extrude(context, id + "F50", {"entities" : qUnion([Q0]), "operationType" : NewBodyOperationType.REMOVE, "oppositeDirection" : true, "depth" : 1.2 * mm});
        }
    });
